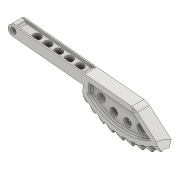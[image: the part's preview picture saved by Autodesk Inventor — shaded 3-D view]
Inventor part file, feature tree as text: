
AUTODESK INVENTOR PART (.ipt)
format: ipt  version: 2020.3 (Build 243373010, 373A)  size: 854,016 bytes
history: native  units: mm (DEFAULTED — no unit token found)
features: sketch x10, other x8, extrude x8, projected_geometry x6, plane x5, fillet x3, delete_face x2, mirror x2, pattern_circular x1
ambient origin geometry x5: Origin, X Axis, Y Axis, Z Axis, Center Point
bodies: Solid1 (feature_tree)
feature tree (45):
  other  "Tooth Plane"
  other  "Base Body Sketch"
  other  "Base Body"
  other  "Base Body2"
  plane  "Work Plane13"
  other  "Tooth"
  pattern_circular  "Tooth Pattern"  Count=40  [1 undecoded]
  plane  "Work Plane14"
  plane  "Work Plane15"
  extrude  "Extrusion1"  TaperAngle=30.0deg  [1 undecoded]
  delete_face  "Delete Face1"
  delete_face  "Delete Face2"
  fillet  "Fillet1"  Radius=138.0mm
  extrude  "Extrusion4"  Depth=6.0mm TaperAngle=0.0deg
  extrude  "Extrusion5"  Depth=6.0mm
  extrude  "Extrusion6"  Depth=6.0mm
  extrude  "Extrusion7"  TaperAngle=0.0deg  [1 undecoded]
  plane  "Work Plane16"
  mirror  "Mirror1"
  fillet  "Fillet2"  [1 undecoded]
  extrude  "Extrusion8"  TaperAngle=0.0deg  [1 undecoded]
  extrude  "Extrusion9"  TaperAngle=0.0deg  [1 undecoded]
  plane  "Work Plane17"
  mirror  "Mirror2"
  fillet  "Fillet3"  Radius=0.785398mm
  extrude  "Extrusion10"  TaperAngle=0.0deg  [1 undecoded]
  sketch  "Sketch19"  dims[d69=0.0mm d73=0.0mm d75=0.785398mm d77=240.0mm d78=24.0mm d79=0.0mm d80=0.0mm d81=0.0mm d82=0.0mm d83=0.785398mm d84=0.0mm d85=180.0deg d86=138.0mm d87=258.0mm d89=24.0mm d90=90.0deg d92=24.0mm d93=138.0mm d94=6.108652mm d98=25.307274mm d99=0.001mm d100=0.0mm d101=20.0mm d118=35.0mm d121=20.0mm d122=125.0mm d123=0.0mm d124=15.0mm d125=20.0mm d126=50.0mm d128=21.25mm d129=10.0mm d131=10.0mm d133=73.028mm d134=0.0mm d135=20.0mm d137=15.0mm d138=24.0mm d139=0.0mm d140=2.5mm d141=5.0mm d142=0.0mm d143=5.0mm d144=10.0mm d146=10.0mm d147=10.0mm d148=7.5mm d149=0.0mm d150=15.0mm d151=40.0mm d153=8.726646mm d155=5.001mm d156=0.0mm d157=2.5mm d158=12.0mm d159=6.0mm d160=0.001mm d161=0.0mm]
  other  "Tooth Sketch"
  sketch  "Sketch8"  dims[d35=90.0deg]
  other  "Srf1"
  sketch  "Sketch9"  dims[d37=-1.651487mm]
  projected_geometry  "Projected Loop1"
  sketch  "Sketch12"  dims[d38=138.0mm]
  sketch  "Sketch13"  dims[d39=3.490659mm]
  sketch  "Sketch14"  dims[d40=10.8mm]
  sketch  "Sketch15"  dims[d41=18.0mm]
  projected_geometry  "Projected Loop2"
  sketch  "Sketch16"  dims[d42=5.654867mm]
  sketch  "Sketch17"  dims[d43=90.0deg d44=400.0mm]
  sketch  "Sketch18"  dims[d46=360.0deg d50=30.0deg d68=138.0mm]
  projected_geometry  "Projected Loop3"
  other  "Pitch Diameter"
  projected_geometry  "Project Cut Edges1"
  projected_geometry  "Project Cut Edges2"
  projected_geometry  "Project Cut Edges3"
note: 7 required parameter values undecoded (feature->parameter linkage not recoverable at this tier; creation-order binding heuristic only, values carry confidence <= 0.55)
